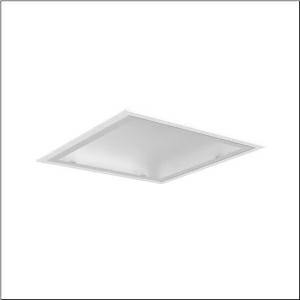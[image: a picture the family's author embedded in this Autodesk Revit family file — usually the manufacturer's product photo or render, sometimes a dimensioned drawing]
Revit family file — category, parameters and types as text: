
# Revit family: mira_r__11_51fr127a461a_fb6f
name_source: partatom
category: Lighting Fixtures
units: mm (PartAtom-declared; Revit-internal decimal feet)

## family parameters
Cut with Voids When Loaded = No
Host = Face
Light Source = No
Part Type = Normal
Room Calculation Point = No
Round Connector Dimension = Use Diameter
Shared = No

## types (1)
- Mira® 11 (1 x LED, 6100 lm, 53 W, 4000K)
    Apparent Load = 53 VA
    CIE Flux Codes = 51 82 97 100 100
    Color Rendering = 80
    Color Temperature = 4000K
    Default Elevation = 1800 mm
    Description = Mira® 11, clean room luminaire, primary light control with reflector, primary optical cover: cover, of toughened safety glass, light emission: direct distribution, primary light characteristic: symmetric, installation type: recessed, LED, rated luminous flux: 6.100lm, luminous efficacy: 115lm/W, light colour: 840, colour temperature: 4000K, control gear: ON/OFF, with terminal, 3-pole, max. 2.5mm², mains connection: 230V, AC, 50/60Hz, rated input power: 53W, luminaire housing, of sheet steel, coated, pure white (RAL 9010), with concealed magnets, module: M625, length: 623mm, width: 623mm, height: 90mm, protection rating (complete): IP65, insulation class (complete): insulation class I (protective earthing), certification: CE, UKCA, permissible operating ambient temperature: -5..+40°C, standard: EN 50419, packaging unit: 1 piece
    Height = 0 mm  [stored 0 ft]
    Lamp = 1 x LED
    Lamp Light Flux = 6100 lm
    Lamp Power = 53 W
    Lamp count = 1
    Length = 625 mm
    Luminous efficacy = 115 lm/W
    Manufacturer = Siteco
    ModVariant = No
    Model = 51FR127A461A
    Mounting Place = Ceiling
    Mounting Type = Recessed
    Number of Poles = 1
    OnlyDefault = Yes
    Power Factor = 1
    Product Name = Mira® 11
    Product group = clean room luminaire | ceiling recessed
    ProductGroupID = 402
    Protection Class = Protection class I
    Protection Degree = IP 65
    RLX_Detail_Level = 1
    RLX_Emergency_Light_Flux = 0 lm
    RLX_Emergency_Type = 0
    RLX_Emergency_Type_DB = No
    RlxData = <blob elided: 19285 chars, md5=9d3699bc>
    Socket = socket
    Standby Power = 0 W
    System Light Flux = 6100 lm
    System Power = 53 W
    Type Comments = Product without accessories
    Type Image = l_1006636.jpg
    URL = http://relux.com
    VarID = ---
    Voltage = 0 V
    Weight = 0.00 kg
    Width = 625 mm

note: [stored X ft] marks values corroborated as IEEE doubles in the binary element streams (Revit-internal decimal feet)

## geometry (parser evidence)
native form markers: Blend x4, Sweep x9
no freeform markers — native parametric forms only
